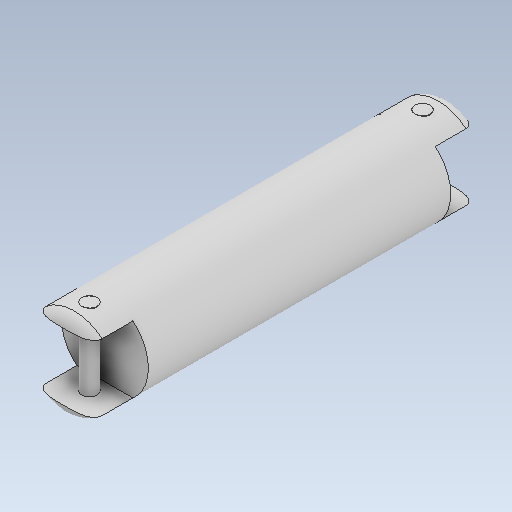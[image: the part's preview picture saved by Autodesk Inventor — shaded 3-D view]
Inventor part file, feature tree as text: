
AUTODESK INVENTOR PART (.ipt)
format: ipt  version: 2021 (Build 250183000, 183)  size: 177,152 bytes
history: native  units: mm
features: extrude x6, sketch x6, projected_geometry x2, fillet x1
ambient origin geometry x8: Origin, YZ Plane, XZ Plane, XY Plane, X Axis, Y Axis, Z Axis, Center Point
bodies: Solid1 (feature_tree)
feature tree (15):
  extrude  "Extrusion1"  Depth=75.0mm TaperAngle=0.0deg
  extrude  "Extrusion2"  Depth=5.0mm
  fillet  "Fillet1"  Radius=3.0mm
  extrude  "Extrusion5"  Depth=10.0mm TaperAngle=0.0deg
  extrude  "Extrusion6"  Depth=13.0mm
  extrude  "Extrusion7"  Depth=8.0mm TaperAngle=0.0deg
  extrude  "Extrusion8"  Depth=6.5mm
  sketch  "Sketch1"  dims[d0=17.0mm d1=75.0mm d2=0.0mm]
  sketch  "Sketch2"  dims[d3=3.0mm d4=5.0mm d5=3.0mm]
  sketch  "Sketch5"  dims[d6=5.0mm d7=10.0mm d8=0.0mm]
  sketch  "Sketch6"  dims[d9=2.0mm d18=13.0mm]
  sketch  "Sketch7"  dims[d19=6.5mm d20=8.0mm d21=0.0mm]
  sketch  "Sketch8"  dims[d22=13.0mm d23=6.5mm d24=8.0mm d25=0.0mm d26=15.0mm d27=2.0mm d28=0.0mm d29=0.0mm d30=15.0mm d31=2.0mm d32=0.0mm d33=0.0mm]
  projected_geometry  "Project Cut Edges1"
  projected_geometry  "Project Cut Edges2"
